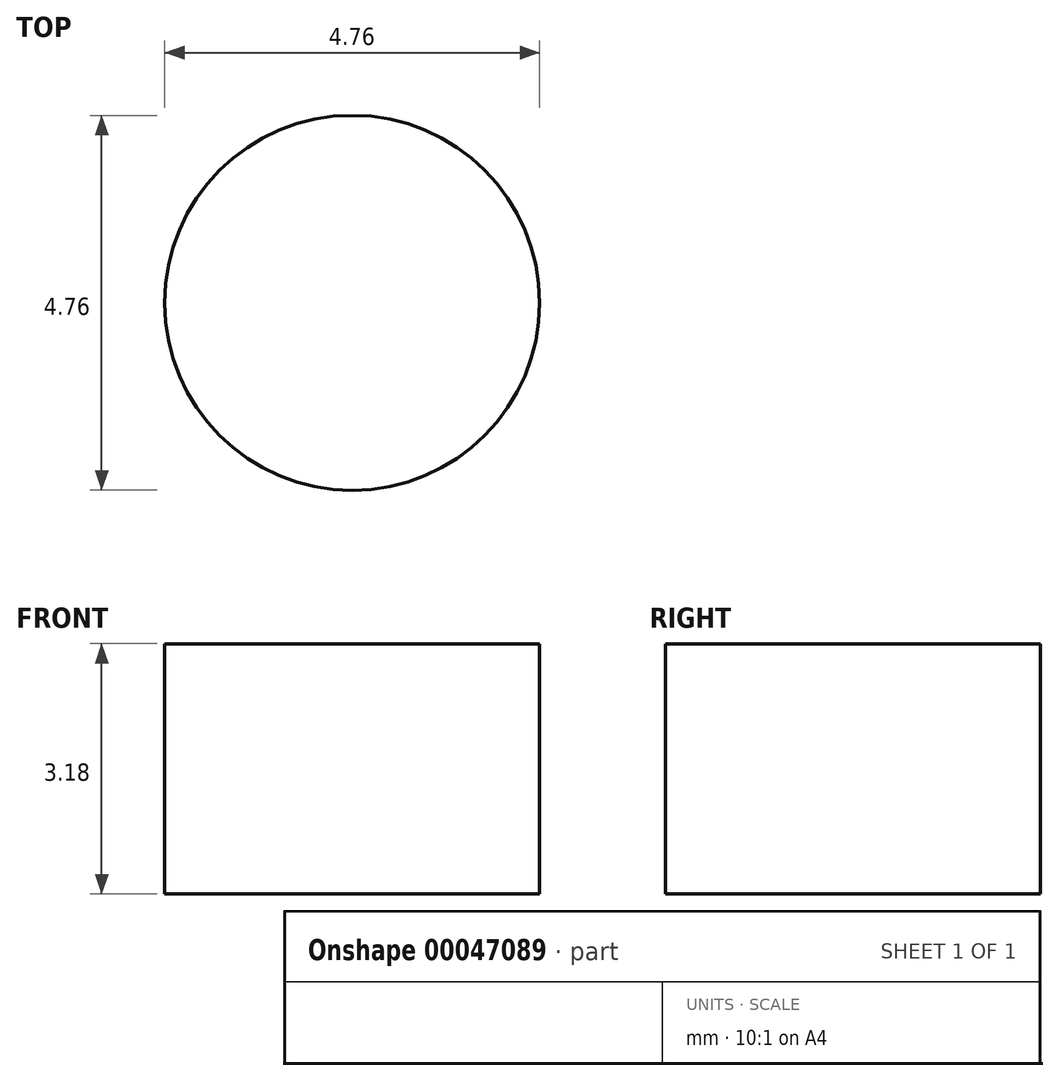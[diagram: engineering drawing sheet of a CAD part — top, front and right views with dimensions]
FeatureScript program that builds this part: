
annotation { "Feature Type Name" : "Feature", "Feature Type Description" : "" }
export const myFeature = defineFeature(function(context is Context, id is Id, definition is map)
    precondition{}
    {
        {
            var Q0;
            Q0=qCreatedBy(makeId("Top.planeOp"),FACE);
            var sketch = newSketch(context, id + "F0", { "sketchPlane" : qUnion([Q0])});
            skLineSegment(sketch, "E0.rect.bottom", {"start": v(25.4, 38.1) * mm, "end": v(-25.4, 38.1) * mm});
            skLineSegment(sketch, "E0.rect.top", {"start": v(25.4, -38.1) * mm, "end": v(-25.4, -38.1) * mm});
            skLineSegment(sketch, "E0.rect.left", {"start": v(25.4, 38.1) * mm, "end": v(25.4, -38.1) * mm});
            skLineSegment(sketch, "E0.rect.right", {"start": v(-25.4, 38.1) * mm, "end": v(-25.4, -38.1) * mm});
            skPoint(sketch, "E0.rect.middle", {"position": v(0, 0) * mm});
            skSolve(sketch);
        }
        {
            var Q0;
            Q0=makeQuery(id+"F0.imprint","IMPRINT",FACE,{"disambiguationData":[TD([[makeQuery(id+"F0.imprint","IMPRINT",EDGE,{"derivedFrom":sQuery(id+"F0.wireOp",EDGE,"E0.rect.bottom")}),1.0]])]});
            extrude(context, id + "F1", {"entities" : qUnion([Q0]), "endBound" : BoundingType.SYMMETRIC, "depth" : 3.17 * mm});
        }
        {
            var Q0;
            Q0=makeQuery(id+"F1.opExtrude","CAP_FACE",FACE,{"disambiguationData":[OSD([sQuery(id+"F0.wireOp",EDGE,"E0.rect.bottom"),sQuery(id+"F0.wireOp",EDGE,"E0.rect.top"),sQuery(id+"F0.wireOp",EDGE,"E0.rect.left"),sQuery(id+"F0.wireOp",EDGE,"E0.rect.right")])],"isStart":false});
            var sketch = newSketch(context, id + "F2", { "sketchPlane" : qUnion([Q0])});
            skLineSegment(sketch, "E1", {"start": v(25.4, -38.1) * mm, "end": v(6.35, -38.1) * mm, "construction": true});
            skLineSegment(sketch, "E2", {"start": v(6.35, -38.1) * mm, "end": v(6.35, -25.4) * mm, "construction": true});
            skCircle(sketch, "E3", {"center": v(6.35, -25.4) * mm, "radius": 2.38 * mm});
            skCircle(sketch, "E4.MirrorC", {"center": v(6.35, 25.4) * mm, "radius": 2.38 * mm});
            skSolve(sketch);
        }
        {
            var Q0;
            Q0=makeQuery(id+"F2.imprint","IMPRINT",FACE,{"disambiguationData":[TD([[makeQuery(id+"F2.imprint","IMPRINT",EDGE,{"derivedFrom":sQuery(id+"F2.wireOp",EDGE,"E4.MirrorC")}),-1.0]])]});
            var Q1;
            Q1=makeQuery(id+"F2.imprint","IMPRINT",FACE,{"disambiguationData":[TD([[makeQuery(id+"F2.imprint","IMPRINT",EDGE,{"derivedFrom":sQuery(id+"F2.wireOp",EDGE,"E3")}),1.0]])]});
            extrude(context, id + "F3", {"entities" : qUnion([Q0, Q1]), "operationType" : NewBodyOperationType.REMOVE, "endBound" : BoundingType.UP_TO_NEXT, "oppositeDirection" : true, "depth" : 25.4 * mm});
        }
    });
